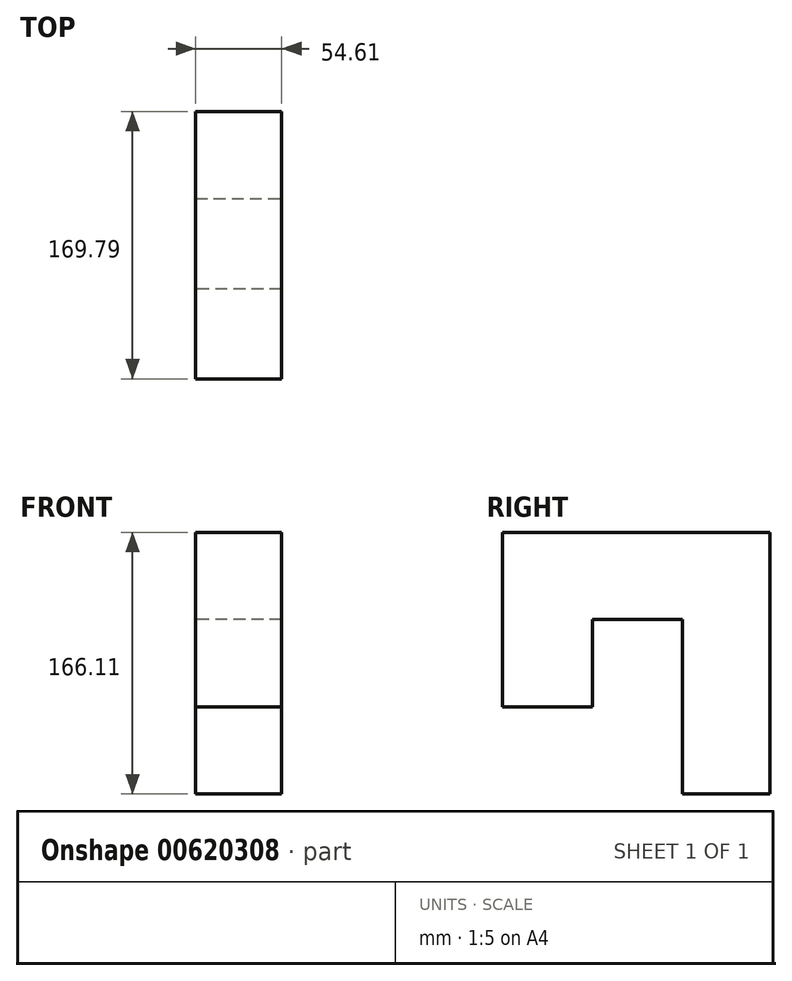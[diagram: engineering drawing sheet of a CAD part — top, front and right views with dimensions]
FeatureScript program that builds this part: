
annotation { "Feature Type Name" : "Feature", "Feature Type Description" : "" }
export const myFeature = defineFeature(function(context is Context, id is Id, definition is map)
    precondition{}
    {
        {
            var Q0;
            Q0=qCreatedBy(makeId("Top.planeOp"),FACE);
            var sketch = newSketch(context, id + "F0", { "sketchPlane" : qUnion([Q0])});
            skLineSegment(sketch, "E0.bottom", {"start": v(0, 0) * mm, "end": v(54.6, 0) * mm});
            skLineSegment(sketch, "E0.top", {"start": v(0, -59.04) * mm, "end": v(54.6, -59.04) * mm});
            skLineSegment(sketch, "E0.left", {"start": v(0, 0) * mm, "end": v(0, -59.04) * mm});
            skLineSegment(sketch, "E0.right", {"start": v(54.6, 0) * mm, "end": v(54.6, -59.04) * mm});
            skSolve(sketch);
        }
        {
            var Q0;
            Q0 = qSketchRegion(id + "F0", true);
            extrude(context, id + "F1", {"entities" : qUnion([Q0]), "depth" : 55.37 * mm, "offsetDistance" : 25.4 * mm});
        }
        {
            var Q0;
            Q0=makeQuery(id+"F1.opExtrude","SWEPT_FACE",FACE,{"disambiguationData":[OSD([sQuery(id+"F0.wireOp",EDGE,"E0.bottom")])]});
            var sketch = newSketch(context, id + "F2", { "sketchPlane" : qUnion([Q0])});
            skLineSegment(sketch, "E1.bottom", {"start": v(0, 0) * mm, "end": v(-54.6, 0) * mm});
            skLineSegment(sketch, "E1.top", {"start": v(0, 55.37) * mm, "end": v(-54.6, 55.37) * mm});
            skLineSegment(sketch, "E1.left", {"start": v(0, 0) * mm, "end": v(0, 55.37) * mm});
            skLineSegment(sketch, "E1.right", {"start": v(-54.6, 0) * mm, "end": v(-54.6, 55.37) * mm});
            skSolve(sketch);
        }
        {
            var Q0;
            Q0 = qSketchRegion(id + "F2", true);
            extrude(context, id + "F3", {"entities" : qUnion([Q0]), "operationType" : NewBodyOperationType.ADD, "depth" : 55.37 * mm, "offsetDistance" : 25.4 * mm});
        }
        {
            var Q0;
            Q0=makeQuery(id+"F1.opExtrude","SWEPT_FACE",FACE,{"disambiguationData":[OSD([sQuery(id+"F0.wireOp",EDGE,"E0.top")])]});
            var sketch = newSketch(context, id + "F4", { "sketchPlane" : qUnion([Q0])});
            skLineSegment(sketch, "E2.bottom", {"start": v(54.6, 0) * mm, "end": v(0, 0) * mm});
            skLineSegment(sketch, "E2.top", {"start": v(54.6, 55.37) * mm, "end": v(0, 55.37) * mm});
            skLineSegment(sketch, "E2.left", {"start": v(54.6, 0) * mm, "end": v(54.6, 55.37) * mm});
            skLineSegment(sketch, "E2.right", {"start": v(0, 0) * mm, "end": v(0, 55.37) * mm});
            skSolve(sketch);
        }
        {
            var Q0;
            Q0 = qSketchRegion(id + "F4", true);
            extrude(context, id + "F5", {"entities" : qUnion([Q0]), "operationType" : NewBodyOperationType.ADD, "depth" : 55.37 * mm, "offsetDistance" : 25.4 * mm});
        }
        {
            var Q0;
            Q0=makeQuery(id+"F5.boolean.opBoolean","MERGE",FACE,{"derivedFrom":[makeQuery(id+"F3.boolean.opBoolean","MERGE",FACE,{"derivedFrom":[makeQuery(id+"F1.opExtrude","CAP_FACE",FACE,{"disambiguationData":[OSD([sQuery(id+"F0.wireOp",EDGE,"E0.bottom"),sQuery(id+"F0.wireOp",EDGE,"E0.top"),sQuery(id+"F0.wireOp",EDGE,"E0.left"),sQuery(id+"F0.wireOp",EDGE,"E0.right")])],"isStart":true}),makeQuery(id+"F3.opExtrude","SWEPT_FACE",FACE,{"disambiguationData":[OSD([sQuery(id+"F2.wireOp",EDGE,"E1.bottom")])]})]}),makeQuery(id+"F5.opExtrude","SWEPT_FACE",FACE,{"disambiguationData":[OSD([sQuery(id+"F4.wireOp",EDGE,"E2.bottom")])]})]});
            var sketch = newSketch(context, id + "F6", { "sketchPlane" : qUnion([Q0])});
            skLineSegment(sketch, "E3.bottom", {"start": v(0, 0) * mm, "end": v(54.6, 0) * mm});
            skLineSegment(sketch, "E3.top", {"start": v(0, -55.37) * mm, "end": v(54.6, -55.37) * mm});
            skLineSegment(sketch, "E3.left", {"start": v(0, 0) * mm, "end": v(0, -55.37) * mm});
            skLineSegment(sketch, "E3.right", {"start": v(54.6, 0) * mm, "end": v(54.6, -55.37) * mm});
            skSolve(sketch);
        }
        {
            var Q0;
            Q0 = qSketchRegion(id + "F6", true);
            extrude(context, id + "F7", {"entities" : qUnion([Q0]), "operationType" : NewBodyOperationType.ADD, "depth" : 55.37 * mm, "offsetDistance" : 25.4 * mm});
        }
        {
            var Q0;
            Q0=makeQuery(id+"F7.opExtrude","CAP_FACE",FACE,{"disambiguationData":[OSD([sQuery(id+"F6.wireOp",EDGE,"E3.bottom"),sQuery(id+"F6.wireOp",EDGE,"E3.top"),sQuery(id+"F6.wireOp",EDGE,"E3.left"),sQuery(id+"F6.wireOp",EDGE,"E3.right")])],"isStart":false});
            var sketch = newSketch(context, id + "F8", { "sketchPlane" : qUnion([Q0])});
            skLineSegment(sketch, "E4.bottom", {"start": v(0, 0) * mm, "end": v(54.6, 0) * mm});
            skLineSegment(sketch, "E4.top", {"start": v(0, -55.37) * mm, "end": v(54.6, -55.37) * mm});
            skLineSegment(sketch, "E4.left", {"start": v(0, 0) * mm, "end": v(0, -55.37) * mm});
            skLineSegment(sketch, "E4.right", {"start": v(54.6, 0) * mm, "end": v(54.6, -55.37) * mm});
            skSolve(sketch);
        }
        {
            var Q0;
            Q0 = qSketchRegion(id + "F8", true);
            extrude(context, id + "F9", {"entities" : qUnion([Q0]), "operationType" : NewBodyOperationType.ADD, "depth" : 55.37 * mm, "offsetDistance" : 25.4 * mm});
        }
        {
            var Q0;
            Q0=makeQuery(id+"F5.boolean.opBoolean","MERGE",FACE,{"derivedFrom":[makeQuery(id+"F3.boolean.opBoolean","MERGE",FACE,{"derivedFrom":[makeQuery(id+"F1.opExtrude","CAP_FACE",FACE,{"disambiguationData":[OSD([sQuery(id+"F0.wireOp",EDGE,"E0.bottom"),sQuery(id+"F0.wireOp",EDGE,"E0.top"),sQuery(id+"F0.wireOp",EDGE,"E0.left"),sQuery(id+"F0.wireOp",EDGE,"E0.right")])],"isStart":true}),makeQuery(id+"F3.opExtrude","SWEPT_FACE",FACE,{"disambiguationData":[OSD([sQuery(id+"F2.wireOp",EDGE,"E1.bottom")])]})]}),makeQuery(id+"F5.opExtrude","SWEPT_FACE",FACE,{"disambiguationData":[OSD([sQuery(id+"F4.wireOp",EDGE,"E2.bottom")])]})]});
            var sketch = newSketch(context, id + "F10", { "sketchPlane" : qUnion([Q0])});
            skLineSegment(sketch, "E5.bottom", {"start": v(54.6, 114.42) * mm, "end": v(0, 114.42) * mm});
            skLineSegment(sketch, "E5.top", {"start": v(54.6, 57.2) * mm, "end": v(0, 57.2) * mm});
            skLineSegment(sketch, "E5.left", {"start": v(54.6, 114.42) * mm, "end": v(54.6, 57.2) * mm});
            skLineSegment(sketch, "E5.right", {"start": v(0, 114.42) * mm, "end": v(0, 57.2) * mm});
            skSolve(sketch);
        }
        {
            var Q0;
            Q0 = qSketchRegion(id + "F10", true);
            extrude(context, id + "F11", {"entities" : qUnion([Q0]), "operationType" : NewBodyOperationType.ADD, "depth" : 55.37 * mm, "offsetDistance" : 25.4 * mm});
        }
    });
